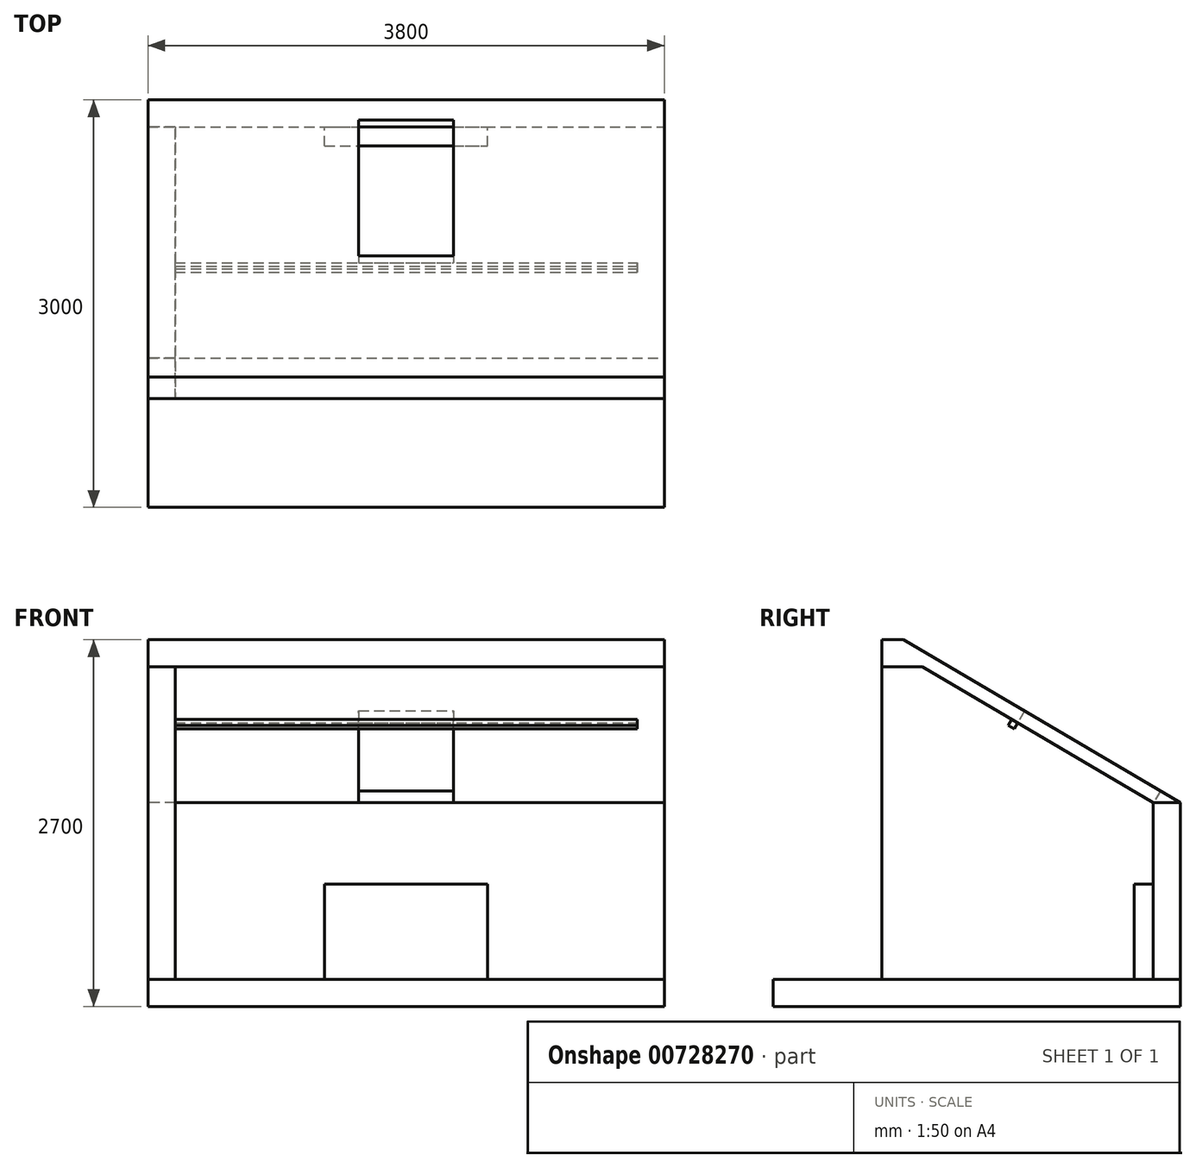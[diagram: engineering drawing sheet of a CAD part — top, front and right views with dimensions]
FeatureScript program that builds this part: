
annotation { "Feature Type Name" : "Feature", "Feature Type Description" : "" }
export const myFeature = defineFeature(function(context is Context, id is Id, definition is map)
    precondition{}
    {
        {
            var Q0;
            Q0=qCreatedBy(makeId("Top.planeOp"),FACE);
            var sketch = newSketch(context, id + "F0", { "sketchPlane" : qUnion([Q0])});
            skLineSegment(sketch, "E0", {"start": v(-159.24, 0) * mm, "end": v(171.07, 0) * mm, "construction": true});
            skLineSegment(sketch, "E1", {"start": v(0, 173.7) * mm, "end": v(0, -221.14) * mm, "construction": true});
            skLineSegment(sketch, "E2.bottom", {"start": v(-1900, 1500) * mm, "end": v(1900, 1500) * mm});
            skLineSegment(sketch, "E2.top", {"start": v(-1900, -1500) * mm, "end": v(1900, -1500) * mm});
            skLineSegment(sketch, "E2.left", {"start": v(-1900, 1500) * mm, "end": v(-1900, -1500) * mm});
            skLineSegment(sketch, "E2.right", {"start": v(1900, 1500) * mm, "end": v(1900, -1500) * mm});
            skSolve(sketch);
        }
        {
            var Q0;
            Q0 = qSketchRegion(id + "F0", true);
            extrude(context, id + "F1", {"entities" : qUnion([Q0]), "endBound" : BoundingType.SYMMETRIC, "depth" : 200 * mm, "offsetDistance" : 25 * mm});
        }
        {
            var Q0;
            Q0=makeQuery(id+"F1.opExtrude","CAP_FACE",FACE,{"disambiguationData":[OSD([sQuery(id+"F0.wireOp",EDGE,"E2.bottom"),sQuery(id+"F0.wireOp",EDGE,"E2.top"),sQuery(id+"F0.wireOp",EDGE,"E2.left"),sQuery(id+"F0.wireOp",EDGE,"E2.right")])],"isStart":false});
            var sketch = newSketch(context, id + "F2", { "sketchPlane" : qUnion([Q0])});
            skLineSegment(sketch, "E3.0", {"start": v(-1900, 1500) * mm, "end": v(-1900, 1300) * mm});
            skLineSegment(sketch, "E4.0", {"start": v(-1900, 1500) * mm, "end": v(1900, 1500) * mm});
            skLineSegment(sketch, "E5", {"start": v(-1900, 1300) * mm, "end": v(1900, 1300) * mm});
            skLineSegment(sketch, "E6.0", {"start": v(1900, 1500) * mm, "end": v(1900, 1300) * mm});
            skPoint(sketch, "E7.orphan", {"position": v(-1900, -1500) * mm});
            skPoint(sketch, "E8.orphan", {"position": v(1900, -1500) * mm});
            skSolve(sketch);
        }
        {
            var Q0;
            Q0 = qSketchRegion(id + "F2", true);
            extrude(context, id + "F3", {"entities" : qUnion([Q0]), "depth" : 1300 * mm, "offsetDistance" : 25 * mm});
        }
        {
            var Q0;
            Q0=makeQuery(id+"F1.opExtrude","SWEPT_FACE",FACE,{"disambiguationData":[OSD([sQuery(id+"F0.wireOp",EDGE,"E2.left")])]});
            var sketch = newSketch(context, id + "F4", { "sketchPlane" : qUnion([Q0])});
            skLineSegment(sketch, "E9.0", {"start": v(-1300, 1400) * mm, "end": v(-1300, 100) * mm});
            skLineSegment(sketch, "E10", {"start": v(700, 2400) * mm, "end": v(400, 2400) * mm});
            skLineSegment(sketch, "E11", {"start": v(400, 2400) * mm, "end": v(-1300, 1400) * mm});
            skPoint(sketch, "E12.orphan", {"position": v(-1500, 100) * mm});
            skLineSegment(sketch, "E13", {"start": v(-1300, 100) * mm, "end": v(700, 100) * mm});
            skLineSegment(sketch, "E14", {"start": v(700, 100) * mm, "end": v(700, 2400) * mm});
            skSolve(sketch);
        }
        {
            var Q0;
            Q0=makeQuery(id+"F4.imprint","IMPRINT",FACE,{"disambiguationData":[TD([[makeQuery(id+"F4.imprint","IMPRINT",EDGE,{"derivedFrom":sQuery(id+"F4.wireOp",EDGE,"E9.0")}),1.0]])]});
            extrude(context, id + "F5", {"entities" : qUnion([Q0]), "oppositeDirection" : true, "depth" : 200 * mm, "offsetDistance" : 25 * mm});
        }
        {
            var Q0;
            Q0=makeQuery(id+"F3.opExtrude","SWEPT_FACE",FACE,{"disambiguationData":[OSD([sQuery(id+"F2.wireOp",EDGE,"E6.0")])]});
            var sketch = newSketch(context, id + "F6", { "sketchPlane" : qUnion([Q0])});
            skLineSegment(sketch, "E15.0", {"start": v(-700, 2400) * mm, "end": v(-400, 2400) * mm});
            skLineSegment(sketch, "E16.0", {"start": v(-400, 2400) * mm, "end": v(1300, 1400) * mm});
            skLineSegment(sketch, "E17.0", {"start": v(1500, 1400) * mm, "end": v(1300, 1400) * mm});
            skLineSegment(sketch, "E18", {"start": v(1500, 1400) * mm, "end": v(-540, 2600) * mm});
            skLineSegment(sketch, "E19", {"start": v(-540, 2600) * mm, "end": v(-700, 2600) * mm});
            skLineSegment(sketch, "E20", {"start": v(-700, 2600) * mm, "end": v(-700, 2400) * mm});
            skSolve(sketch);
        }
        {
            var Q0;
            Q0=makeQuery(id+"F6.imprint","IMPRINT",FACE,{"disambiguationData":[TD([[makeQuery(id+"F6.imprint","IMPRINT",EDGE,{"derivedFrom":sQuery(id+"F6.wireOp",EDGE,"E15.0")}),1.0]])]});
            var Q1;
            Q1=makeQuery(id+"F5.opExtrude","CAP_FACE",FACE,{"disambiguationData":[OSD([sQuery(id+"F4.wireOp",EDGE,"E9.0"),sQuery(id+"F4.wireOp",EDGE,"E10"),sQuery(id+"F4.wireOp",EDGE,"E11"),sQuery(id+"F4.wireOp",EDGE,"E13"),sQuery(id+"F4.wireOp",EDGE,"E14")])],"isStart":true});
            extrude(context, id + "F7", {"entities" : qUnion([Q0]), "endBound" : BoundingType.UP_TO_SURFACE, "oppositeDirection" : true, "depth" : 25 * mm, "endBoundEntityFace" : qUnion([Q1]), "offsetDistance" : 25 * mm});
        }
        {
            var Q0;
            Q0=makeQuery(id+"F7.opExtrude","SWEPT_FACE",FACE,{"disambiguationData":[OSD([sQuery(id+"F6.wireOp",EDGE,"E16.0")])]});
            var sketch = newSketch(context, id + "F8", { "sketchPlane" : qUnion([Q0])});
            skLineSegment(sketch, "E21.bottom", {"start": v(-350, -410.69) * mm, "end": v(350, -410.69) * mm});
            skLineSegment(sketch, "E21.top", {"start": v(-350, 749.31) * mm, "end": v(350, 749.31) * mm});
            skLineSegment(sketch, "E21.left", {"start": v(-350, -410.69) * mm, "end": v(-350, 749.31) * mm});
            skLineSegment(sketch, "E21.right", {"start": v(350, -410.69) * mm, "end": v(350, 749.31) * mm});
            skLineSegment(sketch, "E22.0", {"start": v(-1700, 1561.62) * mm, "end": v(-1700, -410.69) * mm});
            skLineSegment(sketch, "E23.bottom", {"start": v(-1700, 749.31) * mm, "end": v(1700, 749.31) * mm});
            skLineSegment(sketch, "E23.top", {"start": v(-1700, 799.31) * mm, "end": v(1700, 799.31) * mm});
            skLineSegment(sketch, "E23.left", {"start": v(-1700, 749.31) * mm, "end": v(-1700, 799.31) * mm});
            skLineSegment(sketch, "E23.right", {"start": v(1700, 749.31) * mm, "end": v(1700, 799.31) * mm});
            skSolve(sketch);
        }
        {
            var Q0;
            Q0=makeQuery(id+"F8.imprint","IMPRINT",FACE,{"disambiguationData":[TD([[makeQuery(id+"F8.imprint","IMPRINT",EDGE,{"derivedFrom":sQuery(id+"F8.wireOp",EDGE,"E21.bottom")}),1.0]])]});
            extrude(context, id + "F9", {"entities" : qUnion([Q0]), "operationType" : NewBodyOperationType.REMOVE, "endBound" : BoundingType.UP_TO_NEXT, "oppositeDirection" : true, "depth" : 25 * mm, "offsetDistance" : 25 * mm});
        }
        {
            var Q0;
            Q0=makeQuery(id+"F3.opExtrude","SWEPT_FACE",FACE,{"disambiguationData":[OSD([sQuery(id+"F2.wireOp",EDGE,"E5")])]});
            var sketch = newSketch(context, id + "F10", { "sketchPlane" : qUnion([Q0])});
            skLineSegment(sketch, "E24.bottom", {"start": v(-600, 100) * mm, "end": v(600, 100) * mm});
            skLineSegment(sketch, "E24.top", {"start": v(-600, 800) * mm, "end": v(600, 800) * mm});
            skLineSegment(sketch, "E24.left", {"start": v(-600, 100) * mm, "end": v(-600, 800) * mm});
            skLineSegment(sketch, "E24.right", {"start": v(600, 100) * mm, "end": v(600, 800) * mm});
            skSolve(sketch);
        }
        {
            var Q0;
            Q0=makeQuery(id+"F10.imprint","IMPRINT",FACE,{"disambiguationData":[TD([[makeQuery(id+"F10.imprint","IMPRINT",EDGE,{"derivedFrom":sQuery(id+"F10.wireOp",EDGE,"E24.bottom")}),1.0]])]});
            extrude(context, id + "F11", {"entities" : qUnion([Q0]), "depth" : 140 * mm, "offsetDistance" : 25 * mm});
        }
        {
            var Q0;
            Q0=makeQuery(id+"F8.imprint","IMPRINT",FACE,{"disambiguationData":[TD([[makeQuery(id+"F8.imprint","IMPRINT",EDGE,{"derivedFrom":sQuery(id+"F8.wireOp",EDGE,"E23.top")}),-1.0]])]});
            extrude(context, id + "F12", {"entities" : qUnion([Q0]), "depth" : 50 * mm, "offsetDistance" : 25 * mm});
        }
    });
